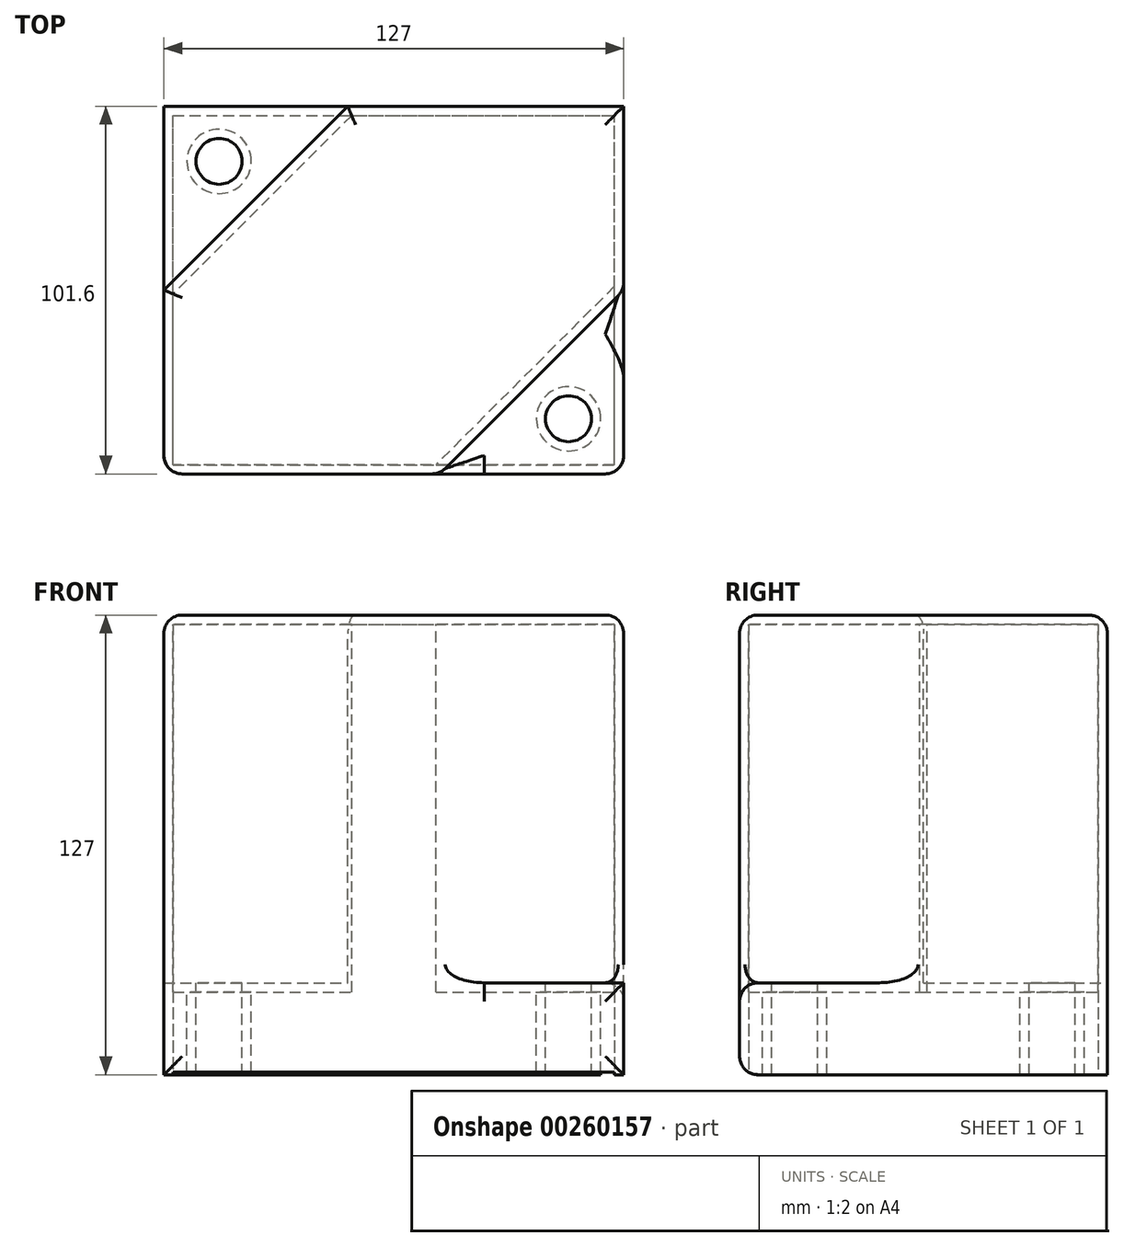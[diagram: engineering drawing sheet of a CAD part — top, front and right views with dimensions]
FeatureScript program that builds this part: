
annotation { "Feature Type Name" : "Feature", "Feature Type Description" : "" }
export const myFeature = defineFeature(function(context is Context, id is Id, definition is map)
    precondition{}
    {
        {
            var Q0;
            Q0=qCreatedBy(makeId("Front.planeOp"),FACE);
            var sketch = newSketch(context, id + "F0", { "sketchPlane" : qUnion([Q0])});
            skLineSegment(sketch, "E0.bottom", {"start": v(-54.48, 54.48) * mm, "end": v(72.52, 54.48) * mm});
            skLineSegment(sketch, "E0.top", {"start": v(-54.48, -72.52) * mm, "end": v(72.52, -72.52) * mm});
            skLineSegment(sketch, "E0.left", {"start": v(-54.48, 54.48) * mm, "end": v(-54.48, -72.52) * mm});
            skLineSegment(sketch, "E0.right", {"start": v(72.52, 54.48) * mm, "end": v(72.52, -72.52) * mm});
            skSolve(sketch);
        }
        {
            var Q0;
            Q0=makeQuery(id+"F0.imprint","IMPRINT",FACE,{"disambiguationData":[TD([[makeQuery(id+"F0.imprint","IMPRINT",EDGE,{"derivedFrom":sQuery(id+"F0.wireOp",EDGE,"E0.bottom")}),-1.0]])]});
            extrude(context, id + "F1", {"entities" : qUnion([Q0]), "depth" : 101.6 * mm});
        }
        {
            var Q0;
            Q0=makeQuery(id+"F1.opExtrude","SWEPT_FACE",FACE,{"disambiguationData":[OSD([sQuery(id+"F0.wireOp",EDGE,"E0.bottom")])]});
            var sketch = newSketch(context, id + "F2", { "sketchPlane" : qUnion([Q0])});
            skLineSegment(sketch, "E1", {"start": v(-54.48, 0) * mm, "end": v(-54.48, -50.8) * mm});
            skLineSegment(sketch, "E2", {"start": v(-54.48, 0) * mm, "end": v(-3.68, 0) * mm});
            skLineSegment(sketch, "E3", {"start": v(-3.68, 0) * mm, "end": v(-54.48, -50.8) * mm});
            skLineSegment(sketch, "E4", {"start": v(72.52, -101.6) * mm, "end": v(21.72, -101.6) * mm});
            skLineSegment(sketch, "E5", {"start": v(72.52, -101.6) * mm, "end": v(72.52, -50.8) * mm});
            skLineSegment(sketch, "E6", {"start": v(72.52, -50.8) * mm, "end": v(21.72, -101.6) * mm});
            skCircle(sketch, "E7", {"center": v(-39.24, -15.24) * mm, "radius": 6.35 * mm});
            skCircle(sketch, "E8", {"center": v(57.28, -86.36) * mm, "radius": 6.35 * mm});
            skSolve(sketch);
        }
        {
            var Q0;
            Q0=makeQuery(id+"F2.imprint","IMPRINT",FACE,{"disambiguationData":[TD([[makeQuery(id+"F2.imprint","IMPRINT",EDGE,{"derivedFrom":sQuery(id+"F2.wireOp",EDGE,"E1")}),-1.0]])]});
            var Q1;
            Q1=makeQuery(id+"F2.imprint","IMPRINT",FACE,{"disambiguationData":[TD([[makeQuery(id+"F2.imprint","IMPRINT",EDGE,{"derivedFrom":sQuery(id+"F2.wireOp",EDGE,"E4")}),1.0]])]});
            extrude(context, id + "F3", {"entities" : qUnion([Q0, Q1]), "operationType" : NewBodyOperationType.REMOVE, "oppositeDirection" : true, "depth" : 101.6 * mm});
        }
        {
            var Q0;
            Q0=makeQuery(id+"F3.boolean.opBoolean","SPLIT",FACE,{"disambiguationData":[TD([makeQuery(id+"F3.opExtrude","SWEPT_FACE",FACE,{"disambiguationData":[OSD([sQuery(id+"F2.wireOp",EDGE,"E7")])]})])],"derivedFrom":makeQuery(id+"F1.opExtrude","SWEPT_FACE",FACE,{"disambiguationData":[OSD([sQuery(id+"F0.wireOp",EDGE,"E0.bottom")])]})});
            var Q1;
            Q1=makeQuery(id+"F3.boolean.opBoolean","SPLIT",FACE,{"disambiguationData":[TD([makeQuery(id+"F3.opExtrude","SWEPT_FACE",FACE,{"disambiguationData":[OSD([sQuery(id+"F2.wireOp",EDGE,"E8")])]})])],"derivedFrom":makeQuery(id+"F1.opExtrude","SWEPT_FACE",FACE,{"disambiguationData":[OSD([sQuery(id+"F0.wireOp",EDGE,"E0.bottom")])]})});
            extrude(context, id + "F4", {"entities" : qUnion([Q0, Q1]), "operationType" : NewBodyOperationType.REMOVE, "oppositeDirection" : true, "depth" : 127.25 * mm});
        }
        {
            var Q0;
            Q0=makeQuery(id+"F1.opExtrude","SWEPT_FACE",FACE,{"disambiguationData":[OSD([sQuery(id+"F0.wireOp",EDGE,"E0.top")])]});
            shell(context, id + "F5", {"entities" : qUnion([Q0]), "thickness" : 2.54 * mm});
        }
        {
            var Q0;
            Q0=makeQuery(id+"F1.opExtrude","CAP_FACE",FACE,{"disambiguationData":[OSD([sQuery(id+"F0.wireOp",EDGE,"E0.bottom"),sQuery(id+"F0.wireOp",EDGE,"E0.top"),sQuery(id+"F0.wireOp",EDGE,"E0.left"),sQuery(id+"F0.wireOp",EDGE,"E0.right")])],"isStart":false});
            var Q1;
            Q1=makeQuery(id+"F3.boolean.opBoolean","COPY",FACE,{"derivedFrom":makeQuery(id+"F3.opExtrude","SWEPT_FACE",FACE,{"disambiguationData":[OSD([sQuery(id+"F2.wireOp",EDGE,"E6")])]})});
            var Q2;
            {var subQ1=sQuery(id+"F0.wireOp",EDGE,"E0.left");var subQ3=sQuery(id+"F0.wireOp",EDGE,"E0.bottom");Q2=makeQuery(id+"F3.boolean.opBoolean","SPLIT",FACE,{"disambiguationData":[TD([makeQuery(id+"F1.opExtrude","SWEPT_FACE",FACE,{"disambiguationData":[OSD([subQ1])]})])],"derivedFrom":makeQuery(id+"F1.opExtrude","SWEPT_FACE",FACE,{"disambiguationData":[OSD([subQ3])]})});}
            fillet(context, id + "F6", {"entities" : qUnion([Q0, Q1, Q2]), "radius" : 5.08 * mm, "tangentPropagation" : true, "allowEdgeOverflow" : false});
        }
    });
